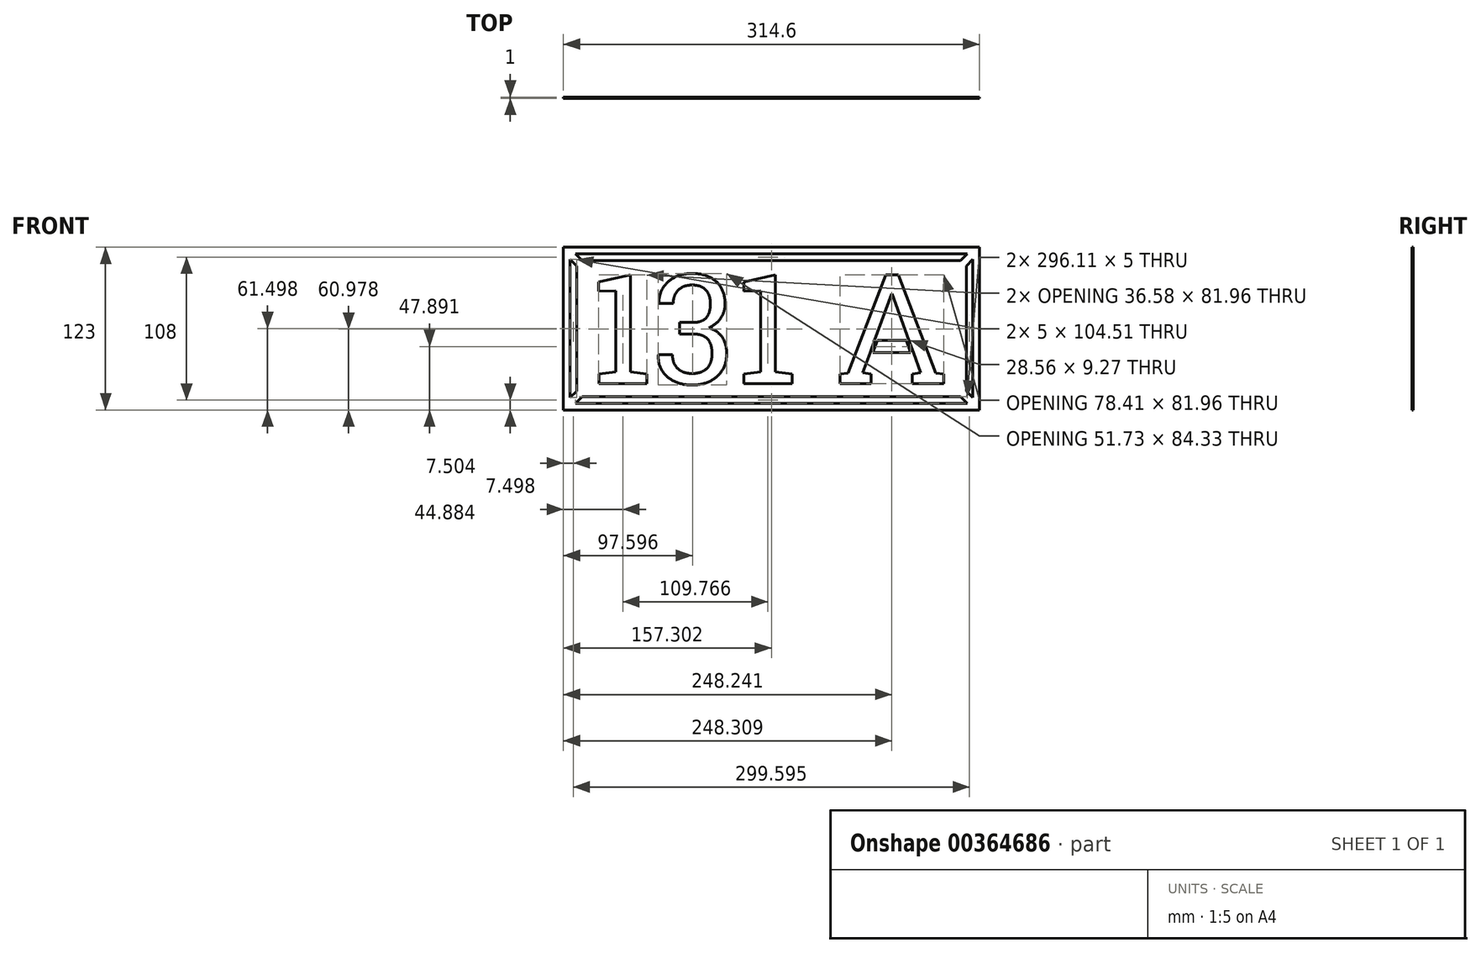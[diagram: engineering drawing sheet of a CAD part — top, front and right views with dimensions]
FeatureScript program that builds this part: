
annotation { "Feature Type Name" : "Feature", "Feature Type Description" : "" }
export const myFeature = defineFeature(function(context is Context, id is Id, definition is map)
    precondition{}
    {
        {
            var Q0;
            Q0=qCreatedBy(makeId("Front.planeOp"),FACE);
            var sketch = newSketch(context, id + "F0", { "sketchPlane" : qUnion([Q0])});
            skText(sketch, "E0", { "text": "131 A", "fontName": "RobotoSlab-Regular.ttf"});
            skLineSegment(sketch, "E1.bottom", {"start": v(-62.38, 80.9) * mm, "end": v(252.22, 80.9) * mm});
            skLineSegment(sketch, "E1.top", {"start": v(-62.38, -42.1) * mm, "end": v(252.22, -42.1) * mm});
            skLineSegment(sketch, "E1.left", {"start": v(-62.38, 80.9) * mm, "end": v(-62.38, -42.1) * mm});
            skLineSegment(sketch, "E1.right", {"start": v(252.22, 80.9) * mm, "end": v(252.22, -42.1) * mm});
            skLineSegment(sketch, "E2", {"start": v(94.92, 60.9) * mm, "end": v(94.92, 80.9) * mm, "construction": true});
            skLineSegment(sketch, "E3", {"start": v(-42.38, 19.4) * mm, "end": v(-62.38, 19.4) * mm, "construction": true});
            const initialGuessF0  = {"E0": [-0.04238, -0.0221, 1, 0, 0.083]};
            skSetInitialGuess(sketch, initialGuessF0);
            skSolve(sketch);
        }
        {
            var Q0;
            Q0 = qSketchRegion(id + "F0", true);
            extrude(context, id + "F1", {"entities" : qUnion([Q0]), "depth" : 1 * mm});
        }
        {
            var Q0;
            Q0=qCreatedBy(makeId("Front.planeOp"),FACE);
            var sketch = newSketch(context, id + "F2", { "sketchPlane" : qUnion([Q0])});
            skLineSegment(sketch, "E4.0.0", {"start": v(186.23, 45.6) * mm, "end": v(185.9, 45.6) * mm});
            skLineSegment(sketch, "E4.0.1", {"start": v(185.9, 45.6) * mm, "end": v(172.94, 10.43) * mm});
            skLineSegment(sketch, "E4.0.2", {"start": v(175.07, 10.43) * mm, "end": v(196.82, 10.43) * mm});
            skLineSegment(sketch, "E4.0.3", {"start": v(198.95, 10.43) * mm, "end": v(186.23, 45.6) * mm});
            skLineSegment(sketch, "E5", {"start": v(172.94, 10.43) * mm, "end": v(169.52, 1.15) * mm});
            skLineSegment(sketch, "E6", {"start": v(169.52, 1.15) * mm, "end": v(171.65, 1.15) * mm});
            skLineSegment(sketch, "E7", {"start": v(171.65, 1.15) * mm, "end": v(175.07, 10.43) * mm});
            skLineSegment(sketch, "E8", {"start": v(196.82, 10.43) * mm, "end": v(200.2, 1.15) * mm});
            skLineSegment(sketch, "E9", {"start": v(200.2, 1.15) * mm, "end": v(202.34, 1.15) * mm});
            skLineSegment(sketch, "E10", {"start": v(202.34, 1.15) * mm, "end": v(198.95, 10.43) * mm});
            skSolve(sketch);
        }
        {
            var Q0;
            Q0 = qSketchRegion(id + "F2", true);
            extrude(context, id + "F3", {"entities" : qUnion([Q0]), "operationType" : NewBodyOperationType.ADD, "depth" : 1 * mm});
        }
        {
            var Q0;
            Q0=makeQuery(id+"F3.boolean.opBoolean","MERGE",FACE,{"derivedFrom":[makeQuery(id+"F1.opExtrude","CAP_FACE",FACE,{"disambiguationData":[OSD([sQuery(id+"F0.wireOp",EDGE,"E0.sketch_text.stroke-0"),sQuery(id+"F0.wireOp",EDGE,"E0.sketch_text.stroke-1"),sQuery(id+"F0.wireOp",EDGE,"E0.sketch_text.stroke-2"),sQuery(id+"F0.wireOp",EDGE,"E0.sketch_text.stroke-3"),sQuery(id+"F0.wireOp",EDGE,"E0.sketch_text.stroke-4"),sQuery(id+"F0.wireOp",EDGE,"E0.sketch_text.stroke-5"),sQuery(id+"F0.wireOp",EDGE,"E0.sketch_text.stroke-6"),sQuery(id+"F0.wireOp",EDGE,"E0.sketch_text.stroke-7"),sQuery(id+"F0.wireOp",EDGE,"E0.sketch_text.stroke-8"),sQuery(id+"F0.wireOp",EDGE,"E0.sketch_text.stroke-9"),sQuery(id+"F0.wireOp",EDGE,"E0.sketch_text.stroke-10"),sQuery(id+"F0.wireOp",EDGE,"E0.sketch_text.stroke-11"),sQuery(id+"F0.wireOp",EDGE,"E0.sketch_text.stroke-12"),sQuery(id+"F0.wireOp",EDGE,"E0.sketch_text.stroke-13"),sQuery(id+"F0.wireOp",EDGE,"E0.sketch_text.stroke-14"),sQuery(id+"F0.wireOp",EDGE,"E0.sketch_text.stroke-15"),sQuery(id+"F0.wireOp",EDGE,"E0.sketch_text.stroke-16"),sQuery(id+"F0.wireOp",EDGE,"E0.sketch_text.stroke-17"),sQuery(id+"F0.wireOp",EDGE,"E0.sketch_text.stroke-18"),sQuery(id+"F0.wireOp",EDGE,"E0.sketch_text.stroke-19"),sQuery(id+"F0.wireOp",EDGE,"E0.sketch_text.stroke-20"),sQuery(id+"F0.wireOp",EDGE,"E0.sketch_text.stroke-21"),sQuery(id+"F0.wireOp",EDGE,"E0.sketch_text.stroke-22"),sQuery(id+"F0.wireOp",EDGE,"E0.sketch_text.stroke-23"),sQuery(id+"F0.wireOp",EDGE,"E0.sketch_text.stroke-24"),sQuery(id+"F0.wireOp",EDGE,"E0.sketch_text.stroke-25"),sQuery(id+"F0.wireOp",EDGE,"E0.sketch_text.stroke-26"),sQuery(id+"F0.wireOp",EDGE,"E0.sketch_text.stroke-27"),sQuery(id+"F0.wireOp",EDGE,"E0.sketch_text.stroke-28"),sQuery(id+"F0.wireOp",EDGE,"E0.sketch_text.stroke-29"),sQuery(id+"F0.wireOp",EDGE,"E0.sketch_text.stroke-30"),sQuery(id+"F0.wireOp",EDGE,"E0.sketch_text.stroke-31"),sQuery(id+"F0.wireOp",EDGE,"E0.sketch_text.stroke-32"),sQuery(id+"F0.wireOp",EDGE,"E0.sketch_text.stroke-33"),sQuery(id+"F0.wireOp",EDGE,"E0.sketch_text.stroke-34"),sQuery(id+"F0.wireOp",EDGE,"E0.sketch_text.stroke-35"),sQuery(id+"F0.wireOp",EDGE,"E0.sketch_text.stroke-36"),sQuery(id+"F0.wireOp",EDGE,"E0.sketch_text.stroke-37"),sQuery(id+"F0.wireOp",EDGE,"E0.sketch_text.stroke-38"),sQuery(id+"F0.wireOp",EDGE,"E0.sketch_text.stroke-39"),sQuery(id+"F0.wireOp",EDGE,"E0.sketch_text.stroke-40"),sQuery(id+"F0.wireOp",EDGE,"E0.sketch_text.stroke-41"),sQuery(id+"F0.wireOp",EDGE,"E0.sketch_text.stroke-42"),sQuery(id+"F0.wireOp",EDGE,"E0.sketch_text.stroke-43"),sQuery(id+"F0.wireOp",EDGE,"E0.sketch_text.stroke-44"),sQuery(id+"F0.wireOp",EDGE,"E0.sketch_text.stroke-45"),sQuery(id+"F0.wireOp",EDGE,"E0.sketch_text.stroke-46"),sQuery(id+"F0.wireOp",EDGE,"E0.sketch_text.stroke-47"),sQuery(id+"F0.wireOp",EDGE,"E0.sketch_text.stroke-48"),sQuery(id+"F0.wireOp",EDGE,"E0.sketch_text.stroke-49"),sQuery(id+"F0.wireOp",EDGE,"E0.sketch_text.stroke-50"),sQuery(id+"F0.wireOp",EDGE,"E0.sketch_text.stroke-51"),sQuery(id+"F0.wireOp",EDGE,"E0.sketch_text.stroke-52"),sQuery(id+"F0.wireOp",EDGE,"E0.sketch_text.stroke-53"),sQuery(id+"F0.wireOp",EDGE,"E0.sketch_text.stroke-54"),sQuery(id+"F0.wireOp",EDGE,"E0.sketch_text.stroke-55"),sQuery(id+"F0.wireOp",EDGE,"E0.sketch_text.stroke-56"),sQuery(id+"F0.wireOp",EDGE,"E0.sketch_text.stroke-57"),sQuery(id+"F0.wireOp",EDGE,"E0.sketch_text.stroke-58"),sQuery(id+"F0.wireOp",EDGE,"E0.sketch_text.stroke-59"),sQuery(id+"F0.wireOp",EDGE,"E0.sketch_text.stroke-60"),sQuery(id+"F0.wireOp",EDGE,"E0.sketch_text.stroke-61"),sQuery(id+"F0.wireOp",EDGE,"E0.sketch_text.stroke-62"),sQuery(id+"F0.wireOp",EDGE,"E0.sketch_text.stroke-63"),sQuery(id+"F0.wireOp",EDGE,"E0.sketch_text.stroke-64"),sQuery(id+"F0.wireOp",EDGE,"E0.sketch_text.stroke-65"),sQuery(id+"F0.wireOp",EDGE,"E0.sketch_text.stroke-66"),sQuery(id+"F0.wireOp",EDGE,"E1.bottom"),sQuery(id+"F0.wireOp",EDGE,"E1.top"),sQuery(id+"F0.wireOp",EDGE,"E1.left"),sQuery(id+"F0.wireOp",EDGE,"E1.right")])],"isStart":false}),makeQuery(id+"F3.opExtrude","CAP_FACE",FACE,{"disambiguationData":[OSD([sQuery(id+"F2.wireOp",EDGE,"C4A256Mw-IY4W-F2Ep-ndjc-PvI8AzWS3f4W"),sQuery(id+"F2.wireOp",EDGE,"lq6LK9Ul-cCF2-wqh6-J8MS-pGRVktOW51gb"),sQuery(id+"F2.wireOp",EDGE,"L6D5S5OT-7Nay-vLrM-aEE6-IF2VT3PDK7c7"),sQuery(id+"F2.wireOp",EDGE,"lhYQio9y-SEwZ-1VLG-pI4h-MgA3alZTeLk2"),sQuery(id+"F2.wireOp",EDGE,"1838ab38-64a2-4bec-9229-2bc4509510da.trimOffspring"),sQuery(id+"F2.wireOp",EDGE,"elt74F9U-NZk3-hABY-3JJY-ZFR74cX8720N"),sQuery(id+"F2.wireOp",EDGE,"Wtc58zkL-DjEk-eIc9-rUso-frQJ0GxbPmb3")])],"isStart":false})]});
            var sketch = newSketch(context, id + "F4", { "sketchPlane" : qUnion([Q0])});
            skLineSegment(sketch, "E11", {"start": v(-53.13, 75.9) * mm, "end": v(242.98, 75.9) * mm});
            skLineSegment(sketch, "E12", {"start": v(242.98, 75.9) * mm, "end": v(237.98, 70.9) * mm});
            skLineSegment(sketch, "E13", {"start": v(237.98, 70.9) * mm, "end": v(-48.13, 70.9) * mm});
            skLineSegment(sketch, "E14", {"start": v(-48.13, 70.9) * mm, "end": v(-53.13, 75.9) * mm});
            skLineSegment(sketch, "E15.MirrorCS", {"start": v(-52.38, -27.86) * mm, "end": v(-57.38, -32.86) * mm});
            skLineSegment(sketch, "E16.MirrorCS", {"start": v(-57.38, 71.66) * mm, "end": v(-57.38, -32.86) * mm});
            skLineSegment(sketch, "E17.MirrorCS", {"start": v(-52.38, 66.66) * mm, "end": v(-57.38, 71.66) * mm});
            skLineSegment(sketch, "E18.MirrorCS", {"start": v(-52.38, -27.86) * mm, "end": v(-52.38, 66.66) * mm});
            skLineSegment(sketch, "E19.MirrorCS", {"start": v(242.22, -27.86) * mm, "end": v(247.22, -32.86) * mm});
            skLineSegment(sketch, "E20.MirrorCS", {"start": v(242.22, -27.86) * mm, "end": v(242.22, 66.66) * mm});
            skLineSegment(sketch, "E21.MirrorCS", {"start": v(242.22, 66.66) * mm, "end": v(247.22, 71.66) * mm});
            skLineSegment(sketch, "E22.MirrorCS", {"start": v(247.22, 71.66) * mm, "end": v(247.22, -32.86) * mm});
            skLineSegment(sketch, "E23.MirrorCS", {"start": v(-48.13, -32.1) * mm, "end": v(-53.13, -37.1) * mm});
            skLineSegment(sketch, "E24.MirrorCS", {"start": v(242.98, -37.1) * mm, "end": v(237.98, -32.1) * mm});
            skLineSegment(sketch, "E25.MirrorCS", {"start": v(237.98, -32.1) * mm, "end": v(-48.13, -32.1) * mm});
            skLineSegment(sketch, "E26.MirrorCS", {"start": v(-53.13, -37.1) * mm, "end": v(242.98, -37.1) * mm});
            skLineSegment(sketch, "E27", {"start": v(94.92, 80.9) * mm, "end": v(94.92, 75.9) * mm, "construction": true});
            skPoint(sketch, "E27.endSnap0", {"position": v(94.92, 80.9) * mm});
            skLineSegment(sketch, "E28", {"start": v(94.92, 75.9) * mm, "end": v(94.92, 70.9) * mm, "construction": true});
            skLineSegment(sketch, "E29", {"start": v(94.92, -32.1) * mm, "end": v(94.92, -37.1) * mm, "construction": true});
            skLineSegment(sketch, "E30", {"start": v(94.92, -37.1) * mm, "end": v(94.92, -42.1) * mm, "construction": true});
            skLineSegment(sketch, "E31", {"start": v(-52.38, 19.4) * mm, "end": v(-57.38, 19.4) * mm, "construction": true});
            skLineSegment(sketch, "E32", {"start": v(-57.38, 19.4) * mm, "end": v(-62.38, 19.4) * mm, "construction": true});
            skLineSegment(sketch, "E33", {"start": v(242.22, 19.4) * mm, "end": v(247.22, 19.4) * mm, "construction": true});
            skPoint(sketch, "E33.startSnap0", {"position": v(247.22, 19.4) * mm});
            skLineSegment(sketch, "E34", {"start": v(247.22, 19.4) * mm, "end": v(252.22, 19.4) * mm, "construction": true});
            skSolve(sketch);
        }
        {
            var Q0;
            Q0 = qSketchRegion(id + "F4", true);
            extrude(context, id + "F5", {"entities" : qUnion([Q0]), "operationType" : NewBodyOperationType.REMOVE, "oppositeDirection" : true, "depth" : 25 * mm});
        }
    });
